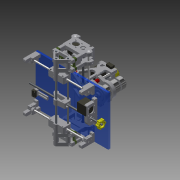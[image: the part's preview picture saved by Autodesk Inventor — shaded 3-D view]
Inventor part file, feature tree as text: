
AUTODESK INVENTOR PART (.ipt)
format: ipt  version: 2013 (Build 170138000, 138)  size: 4,507,648 bytes
history: native  units: mm
features: extrude x175, sketch x157, other x92, projected_geometry x32, fillet x19, mirror x18
ambient origin geometry x8: Origin, YZ Plane, XZ Plane, XY Plane, X Axis, Y Axis, Z Axis, Center Point
feature tree (493):
  other  "vreteno.ipt"
  other  "spodnítyče"
  other  "Bloky"
  extrude  "Vysunutí1"  Depth=80.0mm
  extrude  "Vysunutí2"  Depth=4.2mm
  extrude  "Vysunutí6"  Depth=10.0mm
  extrude  "Vysunutí3"  Depth=30.0mm
  extrude  "Vysunutí4"  Depth=45.0mm
  extrude  "Vysunutí5"  Depth=300.0mm TaperAngle=0.0deg
  extrude  "Vysunutí8"  Depth=4.4mm
  extrude  "Vysunutí33"  Depth=300.0mm TaperAngle=0.0deg
  extrude  "Vysunutí9"  Depth=16.0mm
  extrude  "Vysunutí11"  Depth=100.0mm
  extrude  "Vysunutí13"  Depth=21.5mm
  extrude  "Vysunutí14"  Depth=15.0mm TaperAngle=0.0deg
  extrude  "Vysunutí15"  Depth=10.0mm TaperAngle=0.0deg
  extrude  "Vysunutí16"  Depth=15.0mm TaperAngle=0.0deg
  extrude  "Vysunutí17"  Depth=30.0mm
  extrude  "Vysunutí18"  Depth=300.0mm
  extrude  "Vysunutí20"  Depth=10.0mm
  extrude  "Vysunutí22"  Depth=250.0mm TaperAngle=0.0deg
  extrude  "Vysunutí21"  Depth=15.0mm
  extrude  "Vysunutí23"  Depth=30.0mm
  fillet  "Zaoblení1"  Radius=54.8mm
  extrude  "Vysunutí31"  Depth=110.0mm
  extrude  "Vysunutí32"  Depth=10.0mm TaperAngle=0.0deg
  extrude  "Vysunutí150"  Depth=25.0mm TaperAngle=0.0deg
  extrude  "Vysunutí44"  Depth=15.0mm TaperAngle=0.0deg
  extrude  "Vysunutí45"  Depth=80.0mm TaperAngle=0.0deg
  extrude  "Vysunutí49"  TaperAngle=0.0deg  [1 undecoded]
  extrude  "Vysunutí50"  Depth=10.0mm TaperAngle=0.0deg
  extrude  "Vysunutí51"  Depth=15.0mm TaperAngle=0.0deg
  extrude  "Vysunutí54"  Depth=15.0mm TaperAngle=0.0deg
  extrude  "Vysunutí55"  Depth=15.0mm TaperAngle=0.0deg
  extrude  "Vysunutí56"  Depth=5.0mm
  extrude  "Vysunutí57"  Depth=15.0mm TaperAngle=0.0deg
  extrude  "Vysunutí75"  Depth=15.0mm TaperAngle=0.0deg
  extrude  "Vysunutí68"  Depth=15.0mm TaperAngle=0.0deg
  extrude  "Vysunutí69"  Depth=5.0mm
  extrude  "Vysunutí65"  Depth=8.5mm
  extrude  "Vysunutí66"  Depth=11.2mm
  extrude  "Vysunutí67"  Depth=4.0mm
  fillet  "Zaoblení6"  Radius=46.0mm
  extrude  "Vysunutí71"  Depth=43.0mm
  extrude  "Vysunutí72"  Depth=37.0mm
  extrude  "Vysunutí73"  Depth=31.0mm
  extrude  "Vysunutí74"  Depth=31.0mm
  extrude  "Vysunutí76"  Depth=4.5mm
  extrude  "Vysunutí77"  Depth=80.0mm TaperAngle=0.0deg
  extrude  "Vysunutí78"  Depth=80.0mm TaperAngle=0.0deg
  sketch  "Náčrt73"
  extrude  "Vysunutí82"  Depth=7.0mm
  extrude  "Vysunutí81"  Depth=80.0mm TaperAngle=0.0deg
  extrude  "Vysunutí151"  Depth=20.0mm
  extrude  "Vysunutí228"  Depth=20.0mm
  mirror  "Zrcadlit1"
  mirror  "Zrcadlit2"
  mirror  "Zrcadlit3"
  mirror  "Zrcadlit4"
  mirror  "Zrcadlit5"
  mirror  "Zrcadlit6"
  mirror  "Zrcadlit7"
  mirror  "Zrcadlit9"
  extrude  "Vysunutí84"  Depth=5.0mm TaperAngle=0.0deg
  other  "Posunout těleso1"
  extrude  "Vysunutí85"  Depth=5.0mm TaperAngle=0.0deg
  fillet  "Zaoblení7"  Radius=15.0mm
  extrude  "Vysunutí86"  Depth=23.0mm
  extrude  "Vysunutí87"  Depth=10.0mm TaperAngle=0.0deg
  extrude  "Vysunutí88"  Depth=10.0mm TaperAngle=0.0deg
  extrude  "Vysunutí112"  Depth=23.0mm
  fillet  "Zaoblení8"  Radius=10.0mm
  mirror  "Zrcadlit10"
  mirror  "Zrcadlit11"
  mirror  "Zrcadlit12"
  extrude  "Vysunutí93"  Depth=3.0mm
  mirror  "Zrcadlit13"
  other  "Pracovní rovina26"
  extrude  "Vysunutí121"  Depth=5.0mm
  extrude  "Vysunutí136"  Depth=3.0mm
  extrude  "Vysunutí94"  Depth=3.0mm
  extrude  "Vysunutí95"  Depth=10.0mm TaperAngle=0.0deg
  extrude  "Vysunutí96"  Depth=10.0mm TaperAngle=0.0deg
  extrude  "Vysunutí97"  Depth=4.0mm
  extrude  "Vysunutí98"  Depth=10.0mm TaperAngle=0.0deg
  extrude  "Vysunutí99"  Depth=380.0mm TaperAngle=0.0deg
  extrude  "Vysunutí100"  Depth=14.0mm
  extrude  "Vysunutí101"  Depth=1.0mm
  extrude  "Vysunutí102"  Depth=10.0mm
  fillet  "Zaoblení9"  Radius=1.0mm
  fillet  "Zaoblení10"  Radius=35.0mm
  fillet  "Zaoblení11"  Radius=1.7mm
  extrude  "Vysunutí103"  Depth=14.0mm
  extrude  "Vysunutí104"  Depth=1.0mm
  other  "Pracovní rovina22"
  extrude  "Vysunutí106"  Depth=1.0mm
  other  "Pracovní rovina25"
  extrude  "Vysunutí107"  Depth=14.0mm
  extrude  "Vysunutí119"  Depth=14.0mm
  mirror  "Zrcadlit17"
  extrude  "Vysunutí124"  Depth=20.0mm
  extrude  "Vysunutí125"  Depth=3.0mm
  extrude  "Vysunutí126"  Depth=3.0mm
  extrude  "Vysunutí130"  Depth=15.0mm TaperAngle=0.0deg
  extrude  "Vysunutí127"  Depth=10.0mm TaperAngle=0.0deg
  extrude  "Vysunutí137"  Depth=10.0mm TaperAngle=0.0deg
  mirror  "Zrcadlit18"
  extrude  "Vysunutí135"  Depth=4.0mm
  other  "Kombinovat1"
  extrude  "Vysunutí143"  Depth=10.0mm TaperAngle=0.0deg
  extrude  "Vysunutí144"  Depth=10.0mm TaperAngle=0.0deg
  extrude  "Vysunutí145"  Depth=13.0mm
  extrude  "Vysunutí146"  Depth=10.0mm TaperAngle=0.0deg
  extrude  "Vysunutí147"  Depth=4.0mm
  extrude  "Vysunutí148"  Depth=6.0mm
  extrude  "Vysunutí149"  Depth=6.0mm
  extrude  "Vysunutí153"  Depth=10.0mm TaperAngle=0.0deg
  extrude  "Vysunutí154"  Depth=1.4mm
  extrude  "Vysunutí155"  Depth=1.4mm
  extrude  "Vysunutí156"  Depth=10.0mm TaperAngle=0.0deg
  extrude  "Vysunutí157"  Depth=11.2mm
  extrude  "Vysunutí158"  Depth=4.0mm TaperAngle=0.0deg
  extrude  "Vysunutí159"  Depth=15.0mm TaperAngle=0.0deg
  extrude  "Vysunutí160"  Depth=15.0mm TaperAngle=0.0deg
  extrude  "Vysunutí161"  Depth=11.2mm
  extrude  "Vysunutí162"  Depth=4.0mm TaperAngle=0.0deg
  extrude  "Vysunutí163"  Depth=0.6mm TaperAngle=0.0deg
  extrude  "Vysunutí164"  Depth=15.0mm TaperAngle=0.0deg
  extrude  "Vysunutí165"  Depth=15.0mm TaperAngle=0.0deg
  extrude  "Vysunutí166"  Depth=4.0mm
  extrude  "Vysunutí167"  Depth=300.0mm TaperAngle=0.0deg
  extrude  "Vysunutí168"  Depth=10.0mm
  extrude  "Vysunutí169"  Depth=80.0mm TaperAngle=0.0deg
  extrude  "Vysunutí170"  Depth=14.0mm
  extrude  "Vysunutí171"  Depth=15.0mm
  extrude  "Vysunutí172"  Depth=10.0mm
  extrude  "Vysunutí173"  Depth=15.0mm TaperAngle=0.0deg
  extrude  "Vysunutí174"  Depth=4.0mm
  extrude  "Vysunutí175"  Depth=1.8mm
  extrude  "Vysunutí176"  Depth=40.0mm TaperAngle=0.0deg
  extrude  "Vysunutí179"  Depth=10.0mm TaperAngle=0.0deg
  extrude  "Vysunutí180"  Depth=10.0mm TaperAngle=0.0deg
  extrude  "Vysunutí181"  Depth=2.0mm
  extrude  "Vysunutí182"  Depth=45.0mm TaperAngle=0.0deg
  extrude  "Vysunutí183"  Depth=15.0mm TaperAngle=0.0deg
  extrude  "Vysunutí184"  Depth=45.0mm
  extrude  "Vysunutí185"  Depth=10.0mm TaperAngle=0.0deg
  extrude  "Vysunutí187"  Depth=11.2mm
  extrude  "Vysunutí188"  Depth=4.0mm TaperAngle=0.0deg
  fillet  "Zaoblení12"  Radius=0.6mm
  extrude  "Vysunutí190"  Depth=30.0mm
  extrude  "Vysunutí191"  Depth=15.0mm
  extrude  "Vysunutí192"  Depth=10.0mm
  fillet  "Zaoblení13"  Radius=15.0mm
  extrude  "Vysunutí193"  Depth=10.0mm
  extrude  "Vysunutí194"  Depth=15.0mm
  extrude  "Vysunutí195"  Depth=10.0mm
  extrude  "Vysunutí196"  Depth=15.0mm
  extrude  "Vysunutí197"  Depth=15.0mm TaperAngle=0.0deg
  extrude  "Vysunutí198"  Depth=18.0mm
  extrude  "Vysunutí199"  Depth=4.0mm TaperAngle=0.0deg
  extrude  "Vysunutí200"  Depth=20.0mm
  fillet  "Zaoblení14"  Radius=20.0mm
  extrude  "Vysunutí201"  Depth=10.0mm TaperAngle=0.0deg
  extrude  "Vysunutí202"  Depth=2.5mm
  extrude  "Vysunutí203"  Depth=10.0mm TaperAngle=0.0deg
  extrude  "Vysunutí204"  Depth=20.0mm
  extrude  "Vysunutí205"  Depth=5.0mm
  fillet  "Zaoblení15"  Radius=10.0mm
  extrude  "Vysunutí206"  Depth=7.5mm
  extrude  "Vysunutí207"  Depth=10.0mm TaperAngle=0.0deg
  extrude  "Vysunutí211"  Depth=2.0mm
  extrude  "Vysunutí212"  Depth=1.0mm
  extrude  "Vysunutí213"  Depth=2.0mm TaperAngle=0.0deg
  extrude  "Vysunutí214"  Depth=5.0mm
  fillet  "Zaoblení16"  Radius=5.0mm
  extrude  "Vysunutí215"  Depth=3.0mm
  mirror  "Zrcadlit21"
  extrude  "Vysunutí216"  Depth=3.0mm
  extrude  "Vysunutí217"  Depth=3.0mm
  extrude  "Vysunutí218"  Depth=3.0mm
  fillet  "Zaoblení17"  Radius=16.0mm
  extrude  "Vysunutí220"  Depth=19.0mm
  extrude  "Vysunutí221"  Depth=5.0mm
  extrude  "Vysunutí222"  Depth=60.0mm
  extrude  "Vysunutí223"  Depth=8.1mm
  extrude  "Vysunutí224"  Depth=15.5mm
  extrude  "Vysunutí225"  Depth=50.0mm
  extrude  "Vysunutí226"  Depth=150.0mm TaperAngle=0.0deg
  extrude  "Vysunutí227"  Depth=15.3mm
  extrude  "Vysunutí229"  Depth=49.0mm TaperAngle=0.0deg
  fillet  "Zaoblení18"  Radius=15.0mm
  fillet  "Zaoblení19"  Radius=20.0mm
  extrude  "Vysunutí230"  Depth=35.0mm
  extrude  "Vysunutí231"  Depth=15.3mm
  extrude  "Vysunutí232"  Depth=24.5mm TaperAngle=0.0deg
  extrude  "Vysunutí233"  Depth=12.0mm
  extrude  "Vysunutí234"  Depth=45.0mm
  extrude  "Vysunutí235"  Depth=10.0mm
  extrude  "Vysunutí236"  Depth=15.0mm
  extrude  "Vysunutí237"  Depth=10.0mm
  extrude  "Vysunutí238"  Depth=10.0mm
  fillet  "Zaoblení20"  Radius=10.0mm
  extrude  "Vysunutí239"  Depth=10.0mm
  other  "Pracovní rovina31"
  mirror  "Zrcadlit22"
  extrude  "Vysunutí240"  Depth=10.0mm TaperAngle=0.0deg
  extrude  "Vysunutí241"  Depth=10.0mm TaperAngle=0.0deg
  extrude  "Vysunutí242"  Depth=25.0mm TaperAngle=0.0deg
  extrude  "Vysunutí243"  Depth=25.0mm TaperAngle=0.0deg
  fillet  "Zaoblení21"  Radius=25.0mm
  fillet  "Zaoblení22"  Radius=15.1mm
  mirror  "Zrcadlit23"
  mirror  "Zrcadlit24"
  other  "Závit1"
  other  "Závit2"
  other  "Závit3"
  extrude  "Vysunutí244"  Depth=25.0mm TaperAngle=0.0deg
  extrude  "Vysunutí245"  Depth=11.0mm
  extrude  "Vysunutí246"  Depth=30.0mm TaperAngle=0.0deg
  extrude  "Vysunutí247"  Depth=28.0mm
  fillet  "Zaoblení24"  Radius=30.0mm
  sketch  "Náčrt249"
  extrude  "Vysunutí248"  Depth=43.0mm
  extrude  "Vysunutí249"  Depth=47.0mm
  extrude  "Vysunutí250"  Depth=43.0mm TaperAngle=0.0deg
  sketch  "Náčrt2"
  other  "pohonY"
  sketch  "Náčrt3"
  projected_geometry  "Promítnutá smyčka1"
  projected_geometry  "Promítnutá smyčka2"
  other  "drzaky1"
  sketch  "Náčrt4"
  sketch  "Náčrt5"
  sketch  "Náčrt6"
  other  "stul"
  sketch  "Náčrt9"
  sketch  "Náčrt11"
  other  "drzaky2"
  sketch  "Náčrt14"
  other  "yvozík1"
  other  "yvozík2"
  sketch  "Náčrt18"
  projected_geometry  "Promítnutá smyčka8"
  projected_geometry  "Promítnutá smyčka9"
  sketch  "Náčrt19"
  sketch  "Náčrt20"
  sketch  "Náčrt21"
  sketch  "Náčrt23"
  sketch  "Náčrt24"
  sketch  "Náčrt25"
  sketch  "Náčrt26"
  sketch  "Náčrt27"
  sketch  "Náčrt31"
  sketch  "Náčrt33"
  sketch  "Náčrt41"
  sketch  "Náčrt44"
  sketch  "Náčrt45"
  other  "drzakxvnejsi"
  sketch  "Náčrt48"
  projected_geometry  "Promítnutá smyčka33"
  sketch  "Náčrt50"
  other  "Podložka horni"
  sketch  "Náčrt51"
  other  "posuvx"
  sketch  "Náčrt52"
  other  "tycex"
  sketch  "Náčrt53"
  sketch  "Náčrt54"
  sketch  "Náčrt56"
  sketch  "Náčrt58"
  sketch  "Náčrt60"
  other  "rozpěrka"
  sketch  "Náčrt64"
  projected_geometry  "Promítnutá smyčka40"
  sketch  "Náčrt65"
  sketch  "Náčrt67"
  other  "drzakXvnitrni"
  sketch  "Náčrt70"
  sketch  "Náčrt71"
  sketch  "Náčrt72"
  other  "Pole Podložka horni:1"
  other  "Těleso27"
  other  "Podložka"
  other  "Pole Podložka horni:2"
  other  "Těleso29"
  other  "Pole Podložka horni:3"
  other  "Těleso30"
  other  "Pole Podložka horni:4"
  other  "Těleso31"
  other  "Pole Podložka horni:5"
  other  "srzakxLnirni"
  other  "Pole Podložka horni:6"
  other  "Těleso33"
  other  "Pole Podložka horni:7"
  other  "Těleso34"
  other  "Pole Podložka horni:9"
  other  "Těleso36"
  sketch  "Náčrt77"
  other  "tyceY"
  other  "Těleso1::vreteno.ipt"
  other  "Prvek štítků1"
  sketch  "Náčrt78"
  sketch  "Náčrt79"
  projected_geometry  "Promítnutá smyčka44"
  other  "NohaLZ"
  sketch  "Náčrt80"
  sketch  "Náčrt81"
  sketch  "Náčrt83"
  other  "Pole Podložka horni:10"
  other  "NohaPZ"
  other  "Pole Podložka horni:11"
  other  "NohaLP"
  other  "Pole Podložka horni:12"
  other  "NohaPP"
  sketch  "Náčrt87"
  other  "Těleso43"
  other  "Pole Podložka horni:13"
  other  "Těleso44"
  sketch  "Náčrt88"
  projected_geometry  "Promítnutá smyčka45"
  other  "drzakmotoruY"
  sketch  "Náčrt89"
  sketch  "Náčrt90"
  sketch  "Náčrt91"
  sketch  "Náčrt92"
  sketch  "Náčrt93"
  sketch  "Náčrt94"
  sketch  "Náčrt95"
  sketch  "Náčrt96"
  sketch  "Náčrt97"
  sketch  "Náčrt98"
  other  "vozikxstřed"
  sketch  "Náčrt100"
  other  "tyčeZ"
  sketch  "Náčrt101"
  other  "LM8UU2x Z"
  sketch  "Náčrt116"
  other  "lm8uu X"
  sketch  "Náčrt118"
  other  "vozikxL"
  sketch  "Náčrt119"
  other  "Pole drzakmotoruY:15"
  other  "vozíkxP"
  sketch  "Náčrt120"
  projected_geometry  "Promítnutá smyčka58"
  sketch  "Náčrt128"
  other  "Těleso64"
  sketch  "Náčrt129"
  projected_geometry  "Promítnutá smyčka61"
  sketch  "Náčrt135"
  other  "motorZ"
  sketch  "Náčrt137"
  sketch  "Náčrt138"
  sketch  "Náčrt139"
  other  "drzakmotoruZ"
  sketch  "Náčrt141"
  sketch  "Náčrt142"
  other  "drzakvretenahorní"
  projected_geometry  "Promítnutá smyčka65"
  sketch  "Náčrt144"
  projected_geometry  "Promítnutá smyčka72"
  sketch  "Náčrt145"
  projected_geometry  "Promítnutá smyčka73"
  projected_geometry  "Promítnutá smyčka74"
  projected_geometry  "Promítnutá smyčka79"
  sketch  "Náčrt146"
  other  "drzakxLvnejsi"
  sketch  "Náčrt147"
  projected_geometry  "Promítnutá smyčka83"
  projected_geometry  "Promítnutá smyčka85"
  sketch  "Náčrt148"
  sketch  "Náčrt149"
  sketch  "Náčrt150"
  projected_geometry  "Promítnutá smyčka86"
  sketch  "Náčrt151"
  sketch  "Náčrt154"
  sketch  "Náčrt155"
  sketch  "Náčrt157"
  other  "sroubZ"
  projected_geometry  "Promítnutá smyčka89"
  sketch  "Náčrt158"
  projected_geometry  "Promítnutá smyčka90"
  sketch  "Náčrt159"
  other  "drzakvretenaspodní"
  sketch  "Náčrt160"
  sketch  "Náčrt161"
  sketch  "Náčrt162"
  sketch  "Náčrt163"
  sketch  "Náčrt164"
  sketch  "Náčrt165"
  sketch  "Náčrt166"
  projected_geometry  "Promítnutá smyčka91"
  sketch  "Náčrt167"
  other  "motorX"
  sketch  "Náčrt168"
  sketch  "Náčrt169"
  sketch  "Náčrt172"
  sketch  "Náčrt173"
  projected_geometry  "Promítnutá smyčka92"
  sketch  "Náčrt174"
  sketch  "Náčrt175"
  sketch  "Náčrt176"
  sketch  "Náčrt177"
  sketch  "Náčrt178"
  other  "drzakmatkyx"
  sketch  "Náčrt180"
  sketch  "Náčrt181"
  other  "matkax"
  sketch  "Náčrt182"
  sketch  "Náčrt183"
  sketch  "Náčrt184"
  other  "matkax2"
  sketch  "Náčrt185"
  sketch  "Náčrt186"
  sketch  "Náčrt187"
  sketch  "Náčrt188"
  sketch  "Náčrt189"
  sketch  "Náčrt190"
  sketch  "Náčrt191"
  sketch  "Náčrt192"
  sketch  "Náčrt193"
  sketch  "Náčrt196"
  other  "dorazZ"
  sketch  "Náčrt197"
  sketch  "Náčrt198"
  sketch  "Náčrt201"
  other  "Těleso78"
  sketch  "Náčrt206"
  sketch  "Náčrt207"
  sketch  "Náčrt208"
  sketch  "Náčrt209"
  sketch  "Náčrt210"
  other  "Pole srzakxLnirni:16"
  other  "Těleso79"
  sketch  "Náčrt211"
  sketch  "Náčrt212"
  projected_geometry  "Promítnutá smyčka93"
  sketch  "Náčrt214"
  sketch  "Náčrt217"
  sketch  "Náčrt218"
  sketch  "Náčrt219"
  other  "Těleso80"
  sketch  "Náčrt220"
  sketch  "Náčrt221"
  other  "dorazX"
  sketch  "Náčrt222"
  sketch  "Náčrt223"
  other  "Těleso82"
  projected_geometry  "Promítnutá smyčka94"
  sketch  "Náčrt226"
  sketch  "Náčrt227"
  sketch  "Náčrt228"
  sketch  "Náčrt229"
  sketch  "Náčrt230"
  sketch  "Náčrt231"
  other  "podlozkalm8uuX"
  sketch  "Náčrt232"
  other  "Těleso84"
  sketch  "Náčrt233"
  sketch  "Náčrt234"
  other  "Těleso85"
  sketch  "Náčrt235"
  sketch  "Náčrt236"
  sketch  "Náčrt237"
  sketch  "Náčrt239"
  sketch  "Náčrt240"
  sketch  "Náčrt241"
  other  "manualniovladani"
  sketch  "Náčrt242"
  sketch  "Náčrt245"
  other  "motorY"
  sketch  "Náčrt246"
  sketch  "Náčrt247"
  sketch  "Náčrt248"
  projected_geometry  "Promítnutá smyčka95"
  projected_geometry  "Promítnutá smyčka96"
  projected_geometry  "Promítnutá smyčka97"
  projected_geometry  "Promítnutá smyčka98"
  projected_geometry  "Promítnutá smyčka99"
  projected_geometry  "Promítnutá smyčka100"
  projected_geometry  "Promítnutá smyčka101"
  projected_geometry  "Promítnutá smyčka102"
  other  "Blok1"
  sketch  "Náčrt252"
  other  "motor"
  sketch  "Náčrt253"
  sketch  "Náčrt254"
  other  "vreteno"
  other  "Blok1:1"
  other  "motor:1"
  other  "motor:2"
  other  "motor:3"
note: 1 required parameter value undecoded (feature->parameter linkage not recoverable at this tier; creation-order binding heuristic only, values carry confidence <= 0.55)
